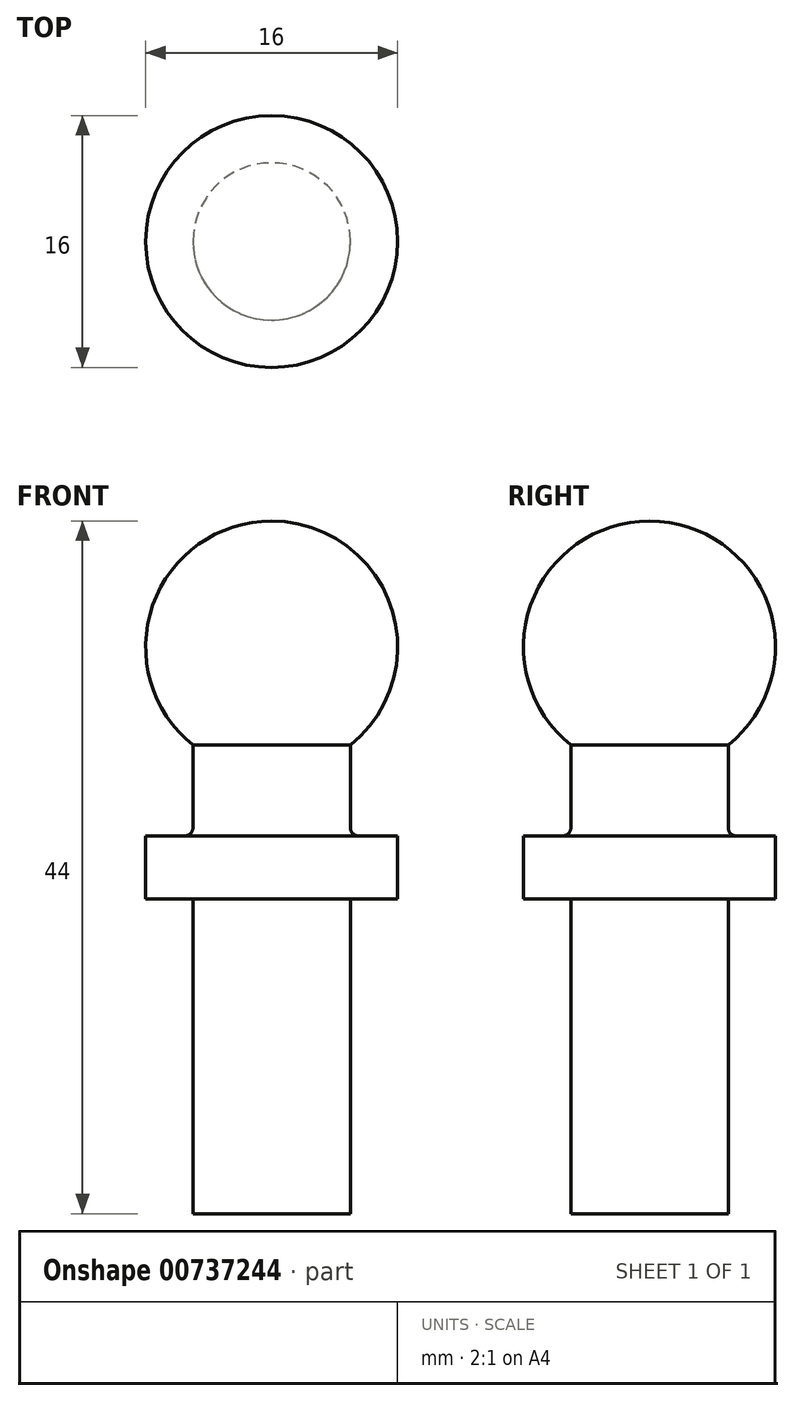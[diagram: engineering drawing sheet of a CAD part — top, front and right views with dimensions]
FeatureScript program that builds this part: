
annotation { "Feature Type Name" : "Feature", "Feature Type Description" : "" }
export const myFeature = defineFeature(function(context is Context, id is Id, definition is map)
    precondition{}
    {
        {
            var Q0;
            Q0=qCreatedBy(makeId("Front.planeOp"),FACE);
            var sketch = newSketch(context, id + "F0", { "sketchPlane" : qUnion([Q0])});
            skArc(sketch, "E0", {"start": v(5, -6.24) * mm, "mid": v(7.55, 2.65) * mm, "end": v(0, 8) * mm});
            skLineSegment(sketch, "E1", {"start": v(0, 12.31) * mm, "end": v(0, -44.07) * mm, "construction": true});
            skLineSegment(sketch, "E2", {"start": v(0, -36) * mm, "end": v(5, -36) * mm});
            skLineSegment(sketch, "E3", {"start": v(5, -36) * mm, "end": v(5, -16) * mm});
            skLineSegment(sketch, "E4", {"start": v(5, -16) * mm, "end": v(8, -16) * mm});
            skLineSegment(sketch, "E5", {"start": v(8, -16) * mm, "end": v(8, -12) * mm});
            skLineSegment(sketch, "E6", {"start": v(8, -12) * mm, "end": v(5.5, -12) * mm});
            skLineSegment(sketch, "E7", {"start": v(5, -11.5) * mm, "end": v(5, -6.24) * mm});
            skPoint(sketch, "E8.visualSharp", {"position": v(5, -12) * mm});
            skArc(sketch, "E8.filletArc", {"start": v(5, -11.5) * mm, "mid": v(5.15, -11.85) * mm, "end": v(5.5, -12) * mm});
            skSolve(sketch);
        }
        {
            var Q0;
            Q0 = qSketchRegion(id + "F0", true);
            var Q1;
            Q1=sQuery(id+"F0.wireOp",EDGE,"E3");
            var Q2;
            Q2=sQuery(id+"F0.wireOp",EDGE,"E6");
            var Q3;
            Q3=sQuery(id+"F0.wireOp",EDGE,"E5");
            var Q4;
            Q4=sQuery(id+"F0.wireOp",EDGE,"E4");
            var Q5;
            Q5=sQuery(id+"F0.wireOp",EDGE,"E7");
            var Q6;
            Q6=sQuery(id+"F0.wireOp",EDGE,"E2");
            var Q7;
            Q7=sQuery(id+"F0.wireOp",EDGE,"E0");
            var Q8;
            Q8=sQuery(id+"F0.wireOp",EDGE,"E8.filletArc");
            var Q9;
            Q9=sQuery(id+"F0.wireOp",EDGE,"E1");
            revolve(context, id + "F1", {"bodyType" : ToolBodyType.SURFACE, "surfaceOperationType" : NewSurfaceOperationType.NEW, "entities" : qUnion([Q0]), "surfaceEntities" : qUnion([Q1, Q2, Q3, Q4, Q5, Q6, Q7, Q8]), "axis" : qUnion([Q9]), "revolveType" : RevolveType.FULL});
        }
    });
